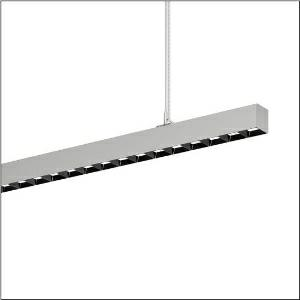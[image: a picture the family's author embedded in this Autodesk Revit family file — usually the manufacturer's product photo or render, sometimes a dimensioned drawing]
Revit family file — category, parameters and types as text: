
# Revit family: silica_r__21_51mx34dc4dsb_5451
name_source: partatom
category: Lighting Fixtures
units: mm (PartAtom-declared; Revit-internal decimal feet)

## family parameters
Cut with Voids When Loaded = No
Host = Face
Light Source = No
Part Type = Normal
Room Calculation Point = No
Round Connector Dimension = Use Diameter
Shared = No

## types (1)
- --- (1 x LED, 19200 lm, 120.3 W, 4000K)
    Apparent Load = 120 VA
    CIE Flux Codes = 74 94 99 56 100
    Color Rendering = 80
    Color Temperature = 4000K
    Default Elevation = 1800 mm
    Description = Silica® 21, office luminaire, primary light control with darklight reflector, of PMMA, black, light emission: direct/indirect distribution, primary light characteristic: asymmetric, installation type: suspended mounting, LED, rated luminous flux: 19.200lm, luminous efficacy: 160lm/W, light colour: 840, colour temperature: 4000K, control gear: DALI 2, with terminal, 3+2-pole, max. 2.5mm², mains connection: 220..240V, AC, 50/60Hz, rated input power: 120.3W, luminaire housing, of aluminium, metallic grey (RAL 9006), length: 3.004mm, width: 53mm, height: 53mm, protection rating (complete): IP20, insulation class (complete): insulation class I (protective earthing), certification: CE, permissible operating ambient temperature: 0..+35°C, standard: EN 50419, packaging unit: 1 piece
    Height = 53 mm
    Lamp = 1 x LED
    Lamp Light Flux = 19200 lm
    Lamp Power = 120.3 W
    Lamp count = 1
    Length = 3004 mm
    Luminous efficacy = 160 lm/W
    Manufacturer = Siteco
    ModVariant = No
    Model = 51MX34DC4DSB
    Mounting Place = Ceiling
    Mounting Type = Pendant
    Number of Poles = 1
    OnlyDefault = Yes
    Power Factor = 1
    Product Name = Silica® 21
    Product group = office luminaire | ceiling pendant
    ProductGroupID = 904
    Protection Class = Protection class I
    Protection Degree = IP 20
    RLX_Detail_Level = 1
    RLX_Emergency_Light_Flux = 0 lm
    RLX_Emergency_Type = 0
    RLX_Emergency_Type_DB = No
    RlxData = <blob elided: 66473 chars, md5=24ba62db>
    Socket = socket
    Standby Power = 0 W
    System Light Flux = 19200 lm
    System Power = 120 W
    Type Comments = factory setting: luminous flux: 100 % | dim-lin: 254 | 418 mA
    Type Image = l_1335859.jpg
    URL = http://relux.com
    VarID = @adj_119884
    Voltage = 0 V
    Weight = 0.00 kg
    Width = 53 mm

## geometry (parser evidence)
native form markers: Blend x4, Sweep x11
no freeform markers — native parametric forms only
